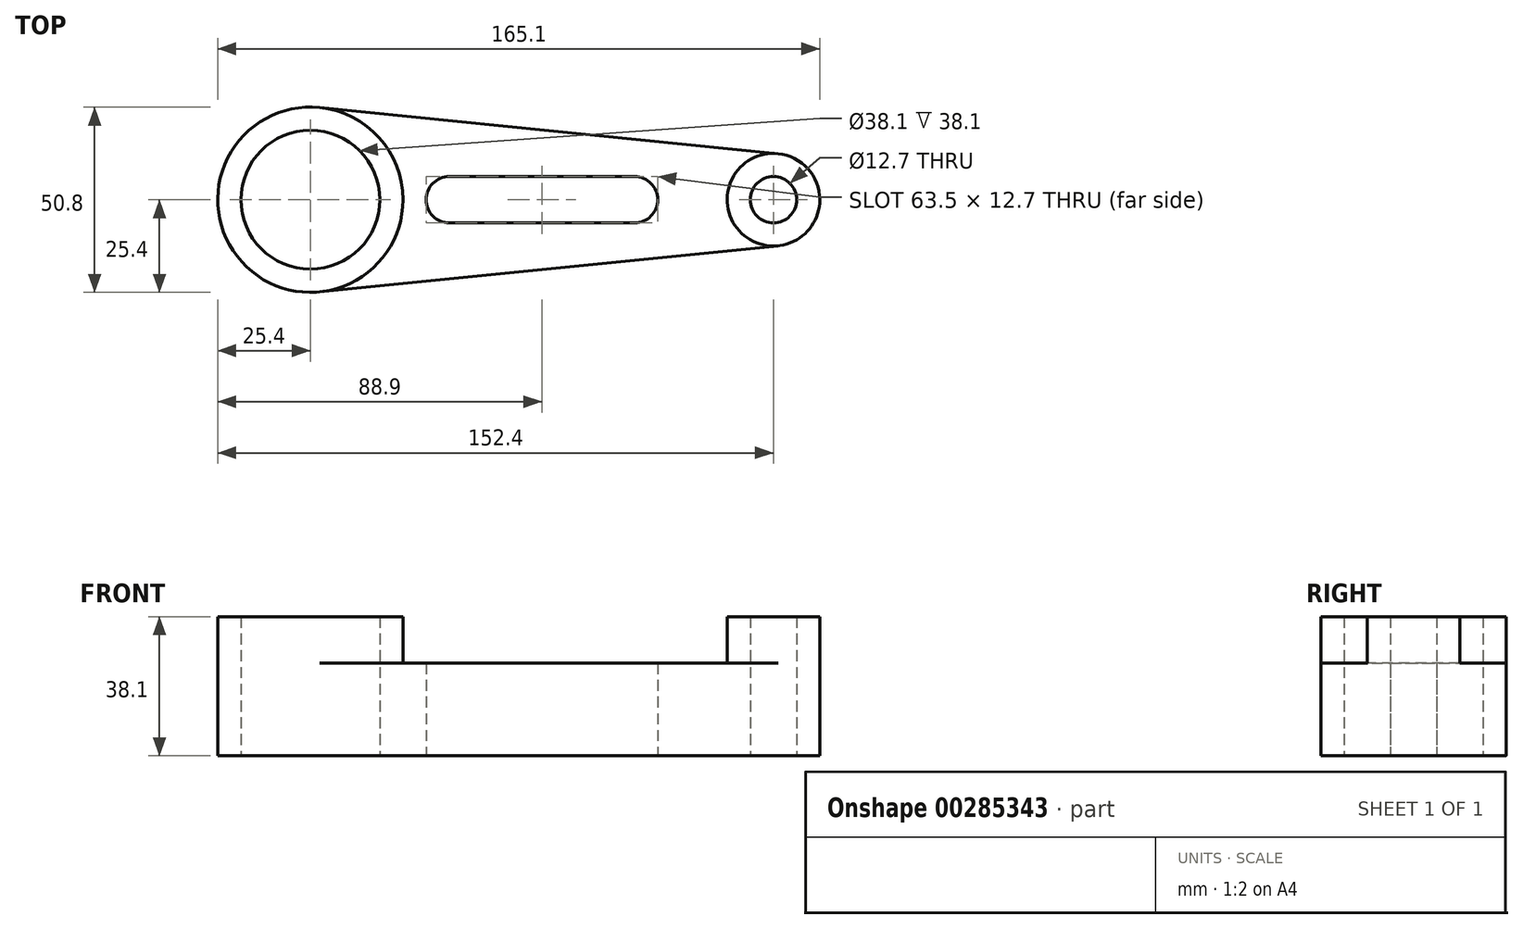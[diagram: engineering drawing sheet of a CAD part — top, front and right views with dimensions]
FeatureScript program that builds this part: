
annotation { "Feature Type Name" : "Feature", "Feature Type Description" : "" }
export const myFeature = defineFeature(function(context is Context, id is Id, definition is map)
    precondition{}
    {
        {
            var Q0;
            Q0=qCreatedBy(makeId("Top.planeOp"),FACE);
            var sketch = newSketch(context, id + "F0", { "sketchPlane" : qUnion([Q0])});
            skArc(sketch, "E0", {"start": v(0, 6.35) * mm, "mid": v(-6.35, 0) * mm, "end": v(0, -6.35) * mm});
            skArc(sketch, "E1", {"start": v(50.8, -6.35) * mm, "mid": v(57.15, 0) * mm, "end": v(50.8, 6.35) * mm});
            skLineSegment(sketch, "E2", {"start": v(0, -6.35) * mm, "end": v(50.8, -6.35) * mm});
            skLineSegment(sketch, "E3", {"start": v(0, 6.35) * mm, "end": v(50.8, 6.35) * mm});
            skCircle(sketch, "E4", {"center": v(88.9, 0) * mm, "radius": 12.7 * mm});
            skCircle(sketch, "E5", {"center": v(88.9, 0) * mm, "radius": 6.35 * mm});
            skCircle(sketch, "E6", {"center": v(-38.1, 0) * mm, "radius": 19.05 * mm});
            skCircle(sketch, "E7", {"center": v(-38.1, 0) * mm, "radius": 25.4 * mm});
            skLineSegment(sketch, "E8", {"start": v(-35.56, -25.27) * mm, "end": v(90.17, -12.64) * mm});
            skLineSegment(sketch, "E9", {"start": v(-35.56, 25.27) * mm, "end": v(90.17, 12.64) * mm});
            skPoint(sketch, "E10.trimOffspring.end.orphan", {"position": v(57.15, 0) * mm});
            skLineSegment(sketch, "E11", {"start": v(57.15, 0) * mm, "end": v(88.9, 0) * mm});
            skSolve(sketch);
        }
        {
            var Q0;
            Q0 = qSketchRegion(id + "F0", true);
            extrude(context, id + "F1", {"entities" : qUnion([Q0]), "depth" : 25.4 * mm});
        }
        {
            var Q0;
            Q0=makeQuery(id+"F0.imprint","IMPRINT",FACE,{"disambiguationData":[TD([[makeQuery(id+"F0.imprint","IMPRINT",EDGE,{"derivedFrom":sQuery(id+"F0.wireOp",EDGE,"E6")}),-1.0]])]});
            var Q1;
            Q1=makeQuery(id+"F0.imprint","IMPRINT",FACE,{"disambiguationData":[TD([[makeQuery(id+"F0.imprint","IMPRINT",EDGE,{"derivedFrom":sQuery(id+"F0.wireOp",EDGE,"E5")}),-1.0]])]});
            extrude(context, id + "F2", {"entities" : qUnion([Q0, Q1]), "operationType" : NewBodyOperationType.ADD, "depth" : 38.1 * mm});
        }
    });
